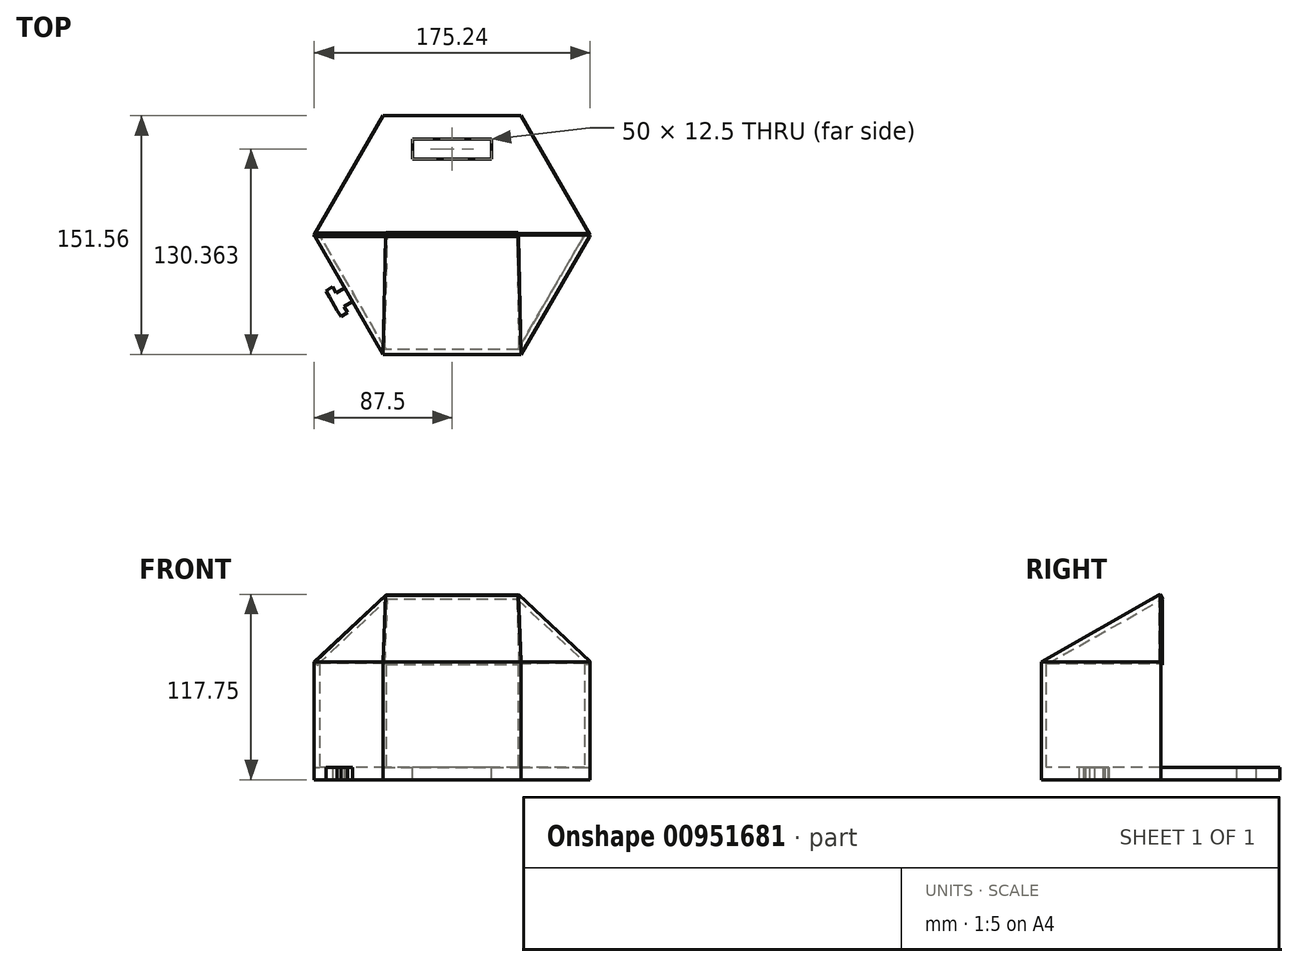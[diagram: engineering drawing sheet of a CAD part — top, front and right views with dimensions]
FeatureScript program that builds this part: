
annotation { "Feature Type Name" : "Feature", "Feature Type Description" : "" }
export const myFeature = defineFeature(function(context is Context, id is Id, definition is map)
    precondition{}
    {
        {
            var Q0;
            Q0=qCreatedBy(makeId("Top.planeOp"),FACE);
            var sketch = newSketch(context, id + "F0", { "sketchPlane" : qUnion([Q0])});
            skCircle(sketch, "E0.cCircle", {"center": v(0, 0) * mm, "radius": 75.78 * mm, "construction": true});
            skLineSegment(sketch, "E0.0", {"start": v(-43.75, 75.78) * mm, "end": v(43.75, 75.78) * mm});
            skLineSegment(sketch, "E0.1", {"start": v(43.75, 75.78) * mm, "end": v(87.5, 0) * mm});
            skLineSegment(sketch, "E0.2", {"start": v(87.5, 0) * mm, "end": v(43.75, -75.78) * mm});
            skLineSegment(sketch, "E0.3", {"start": v(43.75, -75.78) * mm, "end": v(-43.75, -75.78) * mm});
            skLineSegment(sketch, "E0.4", {"start": v(-43.75, -75.78) * mm, "end": v(-87.5, 0) * mm});
            skLineSegment(sketch, "E0.5", {"start": v(-87.5, 0) * mm, "end": v(-43.75, 75.78) * mm});
            skPoint(sketch, "E0.0.midPoint", {"position": v(0, 75.78) * mm});
            skLineSegment(sketch, "E1.0", {"start": v(-84.04, 0) * mm, "end": v(-42.02, 72.78) * mm});
            skLineSegment(sketch, "E1.1", {"start": v(42.02, 72.78) * mm, "end": v(84.04, 0) * mm});
            skLineSegment(sketch, "E1.2", {"start": v(84.04, 0) * mm, "end": v(42.02, -72.78) * mm});
            skLineSegment(sketch, "E1.3", {"start": v(-42.02, 72.78) * mm, "end": v(42.02, 72.78) * mm});
            skLineSegment(sketch, "E1.4", {"start": v(42.02, -72.78) * mm, "end": v(-42.02, -72.78) * mm});
            skLineSegment(sketch, "E1.5", {"start": v(-42.02, -72.78) * mm, "end": v(-84.04, 0) * mm});
            skLineSegment(sketch, "E2", {"start": v(-87.5, 0) * mm, "end": v(-84.04, 0) * mm});
            skLineSegment(sketch, "E3", {"start": v(84.04, 0) * mm, "end": v(87.5, 0) * mm});
            skLineSegment(sketch, "E4", {"start": v(0, 0) * mm, "end": v(0, 72.78) * mm, "construction": true});
            skLineSegment(sketch, "E5", {"start": v(0, 0) * mm, "end": v(42.02, 72.78) * mm, "construction": true});
            skLineSegment(sketch, "E6", {"start": v(0, 0) * mm, "end": v(-42.02, 72.78) * mm, "construction": true});
            skLineSegment(sketch, "E7", {"start": v(0, 36.39) * mm, "end": v(0, 72.78) * mm, "construction": true});
            skLineSegment(sketch, "E8.bottom", {"start": v(25, 48.33) * mm, "end": v(-25, 48.33) * mm});
            skLineSegment(sketch, "E8.top", {"start": v(25, 60.83) * mm, "end": v(-25, 60.83) * mm});
            skLineSegment(sketch, "E8.left", {"start": v(25, 48.33) * mm, "end": v(25, 60.83) * mm});
            skLineSegment(sketch, "E8.right", {"start": v(-25, 48.33) * mm, "end": v(-25, 60.83) * mm});
            skPoint(sketch, "E8.middle", {"position": v(0, 54.58) * mm});
            skLineSegment(sketch, "E9", {"start": v(-65.63, 37.89) * mm, "end": v(-68.13, 33.56) * mm});
            skLineSegment(sketch, "E10.MirrorCS", {"start": v(87.5, 0) * mm, "end": v(43.75, 75.78) * mm});
            skLineSegment(sketch, "E11.MirrorCS", {"start": v(-77.85, -39.32) * mm, "end": v(-68.12, -33.56) * mm});
            skLineSegment(sketch, "E12.MirrorCS", {"start": v(-73.54, -36.77) * mm, "end": v(-75.8, -32.87) * mm});
            skLineSegment(sketch, "E13.MirrorCS", {"start": v(-75.8, -32.87) * mm, "end": v(-80.1, -35.42) * mm});
            skLineSegment(sketch, "E14.MirrorCS", {"start": v(-77.85, -39.32) * mm, "end": v(-80.1, -35.42) * mm});
            skLineSegment(sketch, "E15.MirrorCS", {"start": v(-77.85, -39.32) * mm, "end": v(-72.84, -47.98) * mm});
            skLineSegment(sketch, "E16.MirrorCS", {"start": v(-72.84, -47.98) * mm, "end": v(-70.51, -51.83) * mm});
            skLineSegment(sketch, "E17.MirrorCS", {"start": v(-66.24, -49.24) * mm, "end": v(-70.51, -51.83) * mm});
            skLineSegment(sketch, "E18.MirrorCS", {"start": v(-72.84, -47.98) * mm, "end": v(-63.18, -42.12) * mm});
            skPoint(sketch, "E19.endSnap0", {"position": v(-68.01, -45.05) * mm});
            skLineSegment(sketch, "E20", {"start": v(-66.24, -49.24) * mm, "end": v(-68.57, -45.39) * mm});
            skSolve(sketch);
        }
        {
            var Q0;
            Q0=makeQuery(id+"F0.imprint","IMPRINT",FACE,{"disambiguationData":[TD([[makeQuery(id+"F0.imprint","IMPRINT",EDGE,{"derivedFrom":sQuery(id+"F0.wireOp",EDGE,"E1.0")}),-1.0]])]});
            extrude(context, id + "F1", {"entities" : qUnion([Q0]), "depth" : 8 * mm, "offsetDistance" : 25 * mm});
        }
        {
            var Q0;
            Q0=makeQuery(id+"F0.imprint","IMPRINT",FACE,{"disambiguationData":[TD([[makeQuery(id+"F0.imprint","IMPRINT",EDGE,{"derivedFrom":sQuery(id+"F0.wireOp",EDGE,"E0.2")}),-1.0]])]});
            extrude(context, id + "F2", {"entities" : qUnion([Q0]), "operationType" : NewBodyOperationType.ADD, "depth" : 75 * mm, "offsetDistance" : 25 * mm});
        }
        {
            var Q0;
            Q0=qCreatedBy(makeId("Front.planeOp"),FACE);
            var sketch = newSketch(context, id + "F3", { "sketchPlane" : qUnion([Q0])});
            skLineSegment(sketch, "E21", {"start": v(0, 0) * mm, "end": v(0, 144.27) * mm, "construction": true});
            skLineSegment(sketch, "E22", {"start": v(0, 144.27) * mm, "end": v(-94, 144.27) * mm, "construction": true});
            skLineSegment(sketch, "E23", {"start": v(0, 144.27) * mm, "end": v(81.74, 144.27) * mm});
            skLineSegment(sketch, "E24", {"start": v(0, 0) * mm, "end": v(0, 75) * mm, "construction": true});
            skLineSegment(sketch, "E25", {"start": v(0, 75) * mm, "end": v(0, 114.5) * mm, "construction": true});
            skLineSegment(sketch, "E26", {"start": v(0, 75) * mm, "end": v(-87.5, 75) * mm, "construction": true});
            skLineSegment(sketch, "E27", {"start": v(0, 114.5) * mm, "end": v(42.02, 114.5) * mm, "construction": true});
            skLineSegment(sketch, "E28", {"start": v(0, 114.5) * mm, "end": v(-42.02, 114.5) * mm});
            skLineSegment(sketch, "E29", {"start": v(0, 75) * mm, "end": v(-84.04, 75) * mm, "construction": true});
            skLineSegment(sketch, "E30", {"start": v(-42.02, 114.5) * mm, "end": v(-84.04, 75) * mm});
            skLineSegment(sketch, "E31", {"start": v(-42.02, 114.5) * mm, "end": v(-42.02, 117.5) * mm, "construction": true});
            skLineSegment(sketch, "E32", {"start": v(-42.02, 117.5) * mm, "end": v(-87.5, 75) * mm});
            skLineSegment(sketch, "E33", {"start": v(-42.02, 117.5) * mm, "end": v(0, 117.5) * mm});
            skLineSegment(sketch, "E34.MirrorCS", {"start": v(42.02, 117.5) * mm, "end": v(87.5, 75) * mm});
            skLineSegment(sketch, "E35.MirrorCS", {"start": v(42.02, 114.5) * mm, "end": v(84.04, 75) * mm});
            skLineSegment(sketch, "E36.MirrorCS", {"start": v(42.02, 117.5) * mm, "end": v(0, 117.5) * mm});
            skLineSegment(sketch, "E37.MirrorCS", {"start": v(0, 114.5) * mm, "end": v(42.02, 114.5) * mm});
            skLineSegment(sketch, "E38", {"start": v(87.5, 75) * mm, "end": v(84.04, 75) * mm});
            skLineSegment(sketch, "E39", {"start": v(-84.04, 75) * mm, "end": v(-87.5, 75) * mm});
            skSolve(sketch);
        }
        {
            var Q0;
            Q0=makeQuery(id+"F0.imprint","IMPRINT",FACE,{"disambiguationData":[TD([[makeQuery(id+"F0.imprint","IMPRINT",EDGE,{"derivedFrom":sQuery(id+"F0.wireOp",EDGE,"E0.0")}),-1.0]])]});
            extrude(context, id + "F4", {"entities" : qUnion([Q0]), "operationType" : NewBodyOperationType.ADD, "oppositeDirection" : true, "depth" : -8 * mm, "offsetDistance" : 25 * mm});
        }
        {
            var Q0;
            Q0=makeQuery(id+"F2.opExtrude","CAP_EDGE",EDGE,{"disambiguationData":[OSD([sQuery(id+"F0.wireOp",EDGE,"E0.3")])],"isStart":false});
            var Q1;
            Q1=sQuery(id+"F3.wireOp",VERTEX,"E33.end");
            cPlane(context, id + "F5", {"entities" : qUnion([Q0, Q1]), "cplaneType" : CPlaneType.LINE_ANGLE, "offset" : 25 * mm, "angle" : 0 * degree, "width" : 150 * mm, "height" : 150 * mm});
        }
        {
            var Q0;
            Q0=qCreatedBy(id+"F5.planeOp",FACE);
            var sketch = newSketch(context, id + "F6", { "sketchPlane" : qUnion([Q0])});
            skLineSegment(sketch, "E40", {"start": v(0, 29.4) * mm, "end": v(43.75, 29.4) * mm});
            skLineSegment(sketch, "E41", {"start": v(0, 29.4) * mm, "end": v(-43.75, 29.4) * mm});
            skLineSegment(sketch, "E42", {"start": v(-43.75, 29.4) * mm, "end": v(-42.02, -57.48) * mm});
            skLineSegment(sketch, "E43", {"start": v(43.75, 29.4) * mm, "end": v(42.02, -57.48) * mm});
            skLineSegment(sketch, "E44", {"start": v(-42.02, -57.48) * mm, "end": v(42.02, -57.48) * mm});
            skSolve(sketch);
        }
        {
            var Q0;
            Q0=makeQuery(id+"F6.imprint","IMPRINT",FACE,{"disambiguationData":[TD([[makeQuery(id+"F6.imprint","IMPRINT",EDGE,{"derivedFrom":sQuery(id+"F6.wireOp",EDGE,"E40")}),-1.0]])]});
            extrude(context, id + "F7", {"entities" : qUnion([Q0]), "operationType" : NewBodyOperationType.ADD, "depth" : 3 * mm, "offsetDistance" : 25 * mm});
        }
        {
            var Q0;
            Q0=makeQuery(id+"F3.imprint","IMPRINT",FACE,{"disambiguationData":[TD([[makeQuery(id+"F3.imprint","IMPRINT",EDGE,{"derivedFrom":sQuery(id+"F3.wireOp",EDGE,"E28")}),-1.0]])]});
            extrude(context, id + "F8", {"entities" : qUnion([Q0]), "operationType" : NewBodyOperationType.ADD, "depth" : 1 * mm, "offsetDistance" : 25 * mm});
        }
        {
            var Q0;
            Q0=makeQuery(id+"F8.opExtrude","CAP_EDGE",EDGE,{"disambiguationData":[OSD([sQuery(id+"F3.wireOp",EDGE,"E32")])],"isStart":true});
            var Q1;
            Q1=makeQuery(id+"F7.boolean.opBoolean","MERGE",VERTEX,{"derivedFrom":[makeQuery(id+"F2.opExtrude","CAP_VERTEX",VERTEX,{"disambiguationData":[OSD([sQuery(id+"F0.wireOp",EDGE,"E0.3"),sQuery(id+"F0.wireOp",EDGE,"E0.4")])],"isStart":false}),makeQuery(id+"F7.opExtrude","CAP_VERTEX",VERTEX,{"disambiguationData":[OSD([sQuery(id+"F6.wireOp",EDGE,"E41"),sQuery(id+"F6.wireOp",EDGE,"E42")])],"isStart":true})]});
            cPlane(context, id + "F9", {"entities" : qUnion([Q0, Q1]), "cplaneType" : CPlaneType.LINE_ANGLE, "offset" : 25 * mm, "angle" : 0 * degree, "width" : 150 * mm, "height" : 150 * mm});
        }
        {
            var Q0;
            Q0=qCreatedBy(id+"F9.planeOp",FACE);
            var sketch = newSketch(context, id + "F10", { "sketchPlane" : qUnion([Q0])});
            skLineSegment(sketch, "E45", {"start": v(-25.66, 35.61) * mm, "end": v(30.99, -31.08) * mm});
            skLineSegment(sketch, "E46", {"start": v(-25.66, 35.61) * mm, "end": v(33.23, 55.79) * mm});
            skLineSegment(sketch, "E47", {"start": v(33.23, 55.79) * mm, "end": v(30.99, -31.08) * mm});
            skSolve(sketch);
        }
        {
            var Q0;
            Q0=qSketchRegion(id+"F10",true);
            extrude(context, id + "F11", {"entities" : qUnion([Q0]), "operationType" : NewBodyOperationType.ADD, "depth" : -3 * mm, "offsetDistance" : 25 * mm});
        }
        {
            var Q0;
            Q0=makeQuery(id+"F8.opExtrude","CAP_EDGE",EDGE,{"disambiguationData":[OSD([sQuery(id+"F3.wireOp",EDGE,"E34.MirrorCS")])],"isStart":false});
            var Q1;
            Q1=makeQuery(id+"F7.boolean.opBoolean","MERGE",VERTEX,{"derivedFrom":[makeQuery(id+"F2.opExtrude","CAP_VERTEX",VERTEX,{"disambiguationData":[OSD([sQuery(id+"F0.wireOp",EDGE,"E0.2"),sQuery(id+"F0.wireOp",EDGE,"E0.3")])],"isStart":false}),makeQuery(id+"F7.opExtrude","CAP_VERTEX",VERTEX,{"disambiguationData":[OSD([sQuery(id+"F6.wireOp",EDGE,"E40"),sQuery(id+"F6.wireOp",EDGE,"E43")])],"isStart":true})]});
            cPlane(context, id + "F12", {"entities" : qUnion([Q0, Q1]), "cplaneType" : CPlaneType.LINE_ANGLE, "offset" : 25 * mm, "angle" : 0 * degree, "width" : 150 * mm, "height" : 150 * mm});
        }
        {
            var Q0;
            Q0=qCreatedBy(id+"F12.planeOp",FACE);
            var sketch = newSketch(context, id + "F13", { "sketchPlane" : qUnion([Q0])});
            skLineSegment(sketch, "E48", {"start": v(-32.88, -56.36) * mm, "end": v(25.94, -35.98) * mm});
            skLineSegment(sketch, "E49", {"start": v(25.94, -35.98) * mm, "end": v(-30.94, 30.51) * mm});
            skLineSegment(sketch, "E50", {"start": v(-30.94, 30.51) * mm, "end": v(-32.88, -56.36) * mm});
            skSolve(sketch);
        }
        {
            var Q0;
            Q0=qSketchRegion(id+"F13",true);
            extrude(context, id + "F14", {"entities" : qUnion([Q0]), "operationType" : NewBodyOperationType.ADD, "depth" : 3 * mm, "offsetDistance" : 25 * mm});
        }
        {
            var Q0;
            Q0=makeQuery(id+"F0.imprint","IMPRINT",FACE,{"disambiguationData":[TD([[makeQuery(id+"F0.imprint","IMPRINT",EDGE,{"derivedFrom":sQuery(id+"F0.wireOp",EDGE,"E8.bottom")}),-1.0]])]});
            extrude(context, id + "F15", {"entities" : qUnion([Q0]), "operationType" : NewBodyOperationType.ADD, "depth" : 8 * mm, "offsetDistance" : 25 * mm});
        }
        {
            var Q0;
            {var subQ5=sQuery(id+"F0.wireOp",EDGE,"E13.MirrorCS");Q0=makeQuery(id+"F0.imprint","IMPRINT",FACE,{"disambiguationData":[TD([[makeQuery(id+"F0.imprint","IMPRINT",EDGE,{"derivedFrom":subQ5}),1.0]])]});}
            var Q1;
            {var subQ4=sQuery(id+"F0.wireOp",EDGE,"E15.MirrorCS");Q1=makeQuery(id+"F0.imprint","IMPRINT",FACE,{"disambiguationData":[TD([[makeQuery(id+"F0.imprint","IMPRINT",EDGE,{"derivedFrom":subQ4}),1.0]])]});}
            var Q2;
            {var subQ0=sQuery(id+"F0.wireOp",EDGE,"E16.MirrorCS");Q2=makeQuery(id+"F0.imprint","IMPRINT",FACE,{"disambiguationData":[TD([[makeQuery(id+"F0.imprint","IMPRINT",EDGE,{"derivedFrom":subQ0}),1.0]])]});}
            var Q3;
            {var subQ5=sQuery(id+"F0.wireOp",EDGE,"bff1d7ab-137b-4689-a84f-e4ae87ef17b27.MirrorCS");Q3=makeQuery(id+"F0.imprint","IMPRINT",FACE,{"disambiguationData":[TD([[makeQuery(id+"F0.imprint","IMPRINT",EDGE,{"derivedFrom":subQ5}),-1.0]])]});}
            var Q4;
            {var subQ0=sQuery(id+"F0.wireOp",EDGE,"bff1d7ab-137b-4689-a84f-e4ae87ef17b24.MirrorCS");Q4=makeQuery(id+"F0.imprint","IMPRINT",FACE,{"disambiguationData":[TD([[makeQuery(id+"F0.imprint","IMPRINT",EDGE,{"derivedFrom":subQ0}),-1.0]])]});}
            var Q5;
            {var subQ0=sQuery(id+"F0.wireOp",EDGE,"bff1d7ab-137b-4689-a84f-e4ae87ef17b20.MirrorCS");Q5=makeQuery(id+"F0.imprint","IMPRINT",FACE,{"disambiguationData":[TD([[makeQuery(id+"F0.imprint","IMPRINT",EDGE,{"derivedFrom":subQ0}),1.0]])]});}
            extrude(context, id + "F16", {"entities" : qUnion([Q0, Q1, Q2, Q3, Q4, Q5]), "operationType" : NewBodyOperationType.ADD, "depth" : 8 * mm, "offsetDistance" : 25 * mm});
        }
        {
            var Q0;
            Q0=makeQuery(id+"F0.imprint","IMPRINT",FACE,{"disambiguationData":[TD([[makeQuery(id+"F0.imprint","IMPRINT",EDGE,{"derivedFrom":sQuery(id+"F0.wireOp",EDGE,"E8.bottom")}),-1.0]])]});
            extrude(context, id + "F17", {"entities" : qUnion([Q0]), "operationType" : NewBodyOperationType.REMOVE, "endBound" : BoundingType.SYMMETRIC, "oppositeDirection" : true, "depth" : 25 * mm, "offsetDistance" : 25 * mm});
        }
    });
